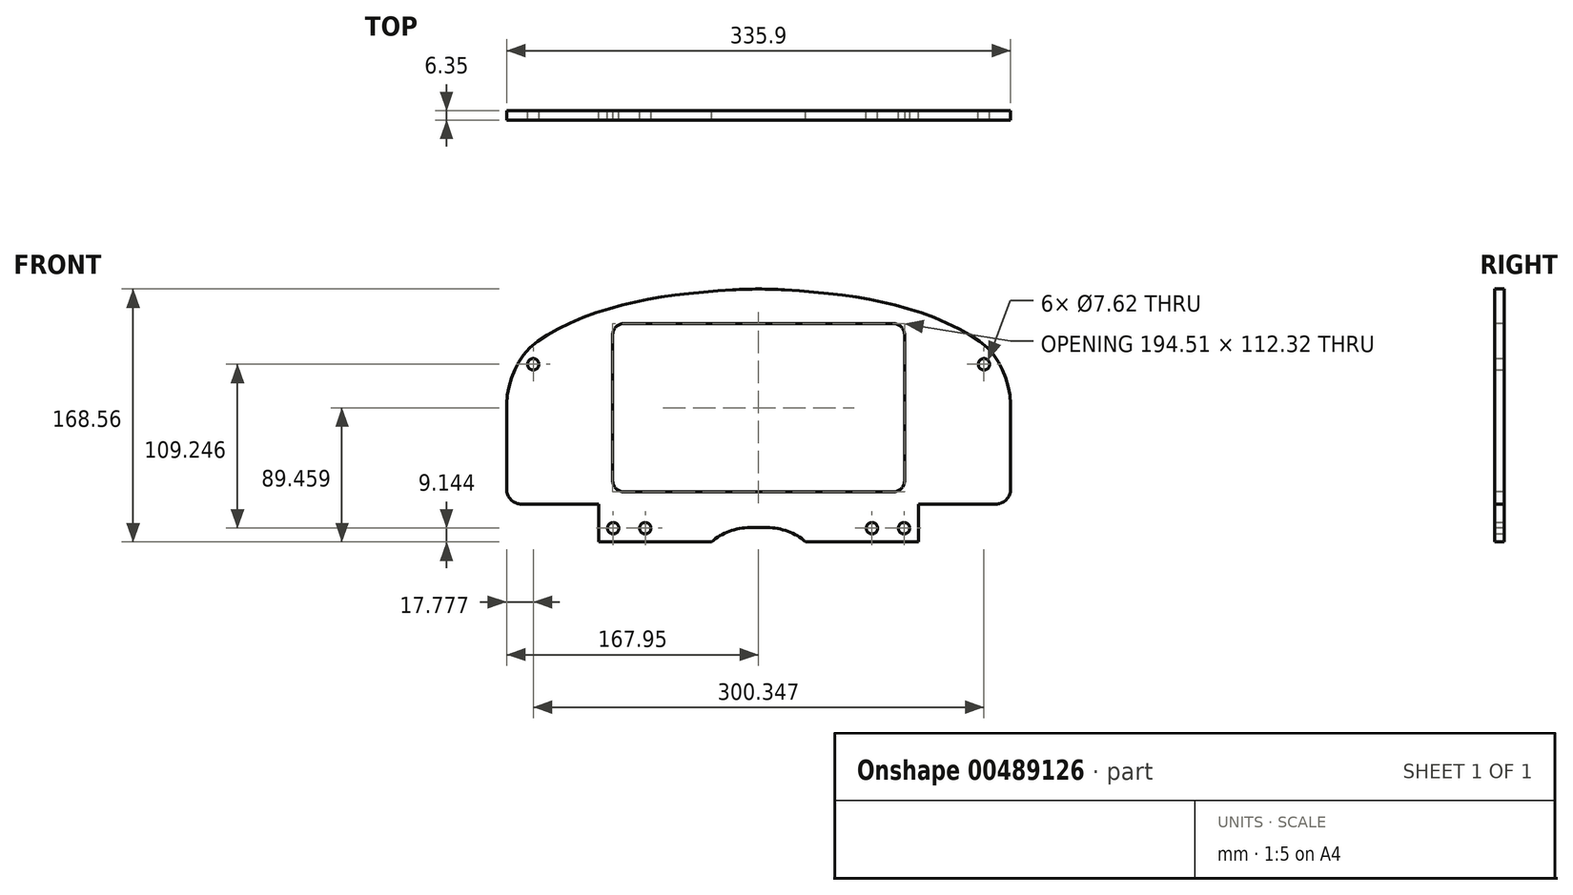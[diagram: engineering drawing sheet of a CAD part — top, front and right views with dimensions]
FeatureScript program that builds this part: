
annotation { "Feature Type Name" : "Feature", "Feature Type Description" : "" }
export const myFeature = defineFeature(function(context is Context, id is Id, definition is map)
    precondition{}
    {
        {
            var Q0;
            Q0=qCreatedBy(makeId("Front.planeOp"),FACE);
            var sketch = newSketch(context, id + "F0", { "sketchPlane" : qUnion([Q0])});
            skLineSegment(sketch, "E0", {"start": v(-160.02, 0) * mm, "end": v(160.02, 0) * mm});
            skLineSegment(sketch, "E1", {"start": v(-31.43, -64.77) * mm, "end": v(-106.52, -64.77) * mm});
            skLineSegment(sketch, "E2", {"start": v(-106.52, -64.77) * mm, "end": v(-106.52, -39.6) * mm});
            skLineSegment(sketch, "E3", {"start": v(-106.52, -39.6) * mm, "end": v(-167.95, -39.6) * mm});
            skLineSegment(sketch, "E4", {"start": v(-167.95, -39.6) * mm, "end": v(-167.95, 26.96) * mm});
            skLineSegment(sketch, "E5", {"start": v(0, 0) * mm, "end": v(0, 118.4) * mm, "construction": true});
            skLineSegment(sketch, "E6", {"start": v(0, 118.4) * mm, "end": v(0, -81.7) * mm, "construction": true});
            skLineSegment(sketch, "E7", {"start": v(0, -55.25) * mm, "end": v(-5.83, -55.25) * mm});
            skArc(sketch, "E8", {"start": v(-5.83, -55.25) * mm, "mid": v(-19.49, -57.7) * mm, "end": v(-31.43, -64.77) * mm});
            skFitSpline(sketch, "E9", {"points": [v(0, 104.31) * mm, v(-59.59, 99.2) * mm, v(-109.08, 87.67) * mm, v(-150.03, 66.77) * mm, v(-162.83, 48.85) * mm, v(-167.95, 26.96) * mm], "startDerivative": vector(-246.06, -15.43) * mm, "endDerivative": vector(0, -151.52) * mm});
            skFitSpline(sketch, "E10.MirrorCS", {"points": [v(0, 104.31) * mm, v(59.59, 99.2) * mm, v(109.08, 87.67) * mm, v(150.03, 66.77) * mm, v(162.83, 48.85) * mm, v(167.95, 26.96) * mm], "startDerivative": vector(246.06, -15.43) * mm, "endDerivative": vector(0, -151.52) * mm});
            skLineSegment(sketch, "E11.MirrorCS", {"start": v(167.95, -39.6) * mm, "end": v(167.95, 26.96) * mm});
            skLineSegment(sketch, "E12.MirrorCS", {"start": v(106.52, -39.6) * mm, "end": v(167.95, -39.6) * mm});
            skLineSegment(sketch, "E13.MirrorCS", {"start": v(106.52, -64.77) * mm, "end": v(106.52, -39.6) * mm});
            skLineSegment(sketch, "E14.MirrorCS", {"start": v(31.43, -64.77) * mm, "end": v(106.52, -64.77) * mm});
            skArc(sketch, "E15.MirrorCS", {"start": v(5.83, -55.25) * mm, "mid": v(19.49, -57.7) * mm, "end": v(31.43, -64.77) * mm});
            skLineSegment(sketch, "E16.MirrorCS", {"start": v(0, -55.25) * mm, "end": v(5.83, -55.25) * mm});
            skCircle(sketch, "E17", {"center": v(-96.87, -55.63) * mm, "radius": 3.81 * mm});
            skCircle(sketch, "E18", {"center": v(-75.53, -55.63) * mm, "radius": 3.81 * mm});
            skCircle(sketch, "E19", {"center": v(75.53, -55.63) * mm, "radius": 3.81 * mm});
            skCircle(sketch, "E20", {"center": v(96.87, -55.63) * mm, "radius": 3.81 * mm});
            skCircle(sketch, "E21", {"center": v(150.17, 53.62) * mm, "radius": 3.81 * mm});
            skCircle(sketch, "E22", {"center": v(-150.17, 53.62) * mm, "radius": 3.81 * mm});
            skSolve(sketch);
        }
        {
            var Q0;
            Q0=makeQuery(id+"F0.imprint","IMPRINT",FACE,{"disambiguationData":[TD([[makeQuery(id+"F0.imprint","IMPRINT",EDGE,{"derivedFrom":sQuery(id+"F0.wireOp",EDGE,"E1")}),-1.0]])]});
            extrude(context, id + "F1", {"entities" : qUnion([Q0]), "depth" : 6.35 * mm});
        }
        {
            var Q0;
            Q0=makeQuery(id+"F1.opExtrude","SWEPT_EDGE",EDGE,{"disambiguationData":[OSD([sQuery(id+"F0.wireOp",EDGE,"E11.MirrorCS"),sQuery(id+"F0.wireOp",EDGE,"E12.MirrorCS")])]});
            var Q1;
            Q1=makeQuery(id+"F1.opExtrude","SWEPT_EDGE",EDGE,{"disambiguationData":[OSD([sQuery(id+"F0.wireOp",EDGE,"E3"),sQuery(id+"F0.wireOp",EDGE,"E4")])]});
            fillet(context, id + "F2", {"entities" : qUnion([Q0, Q1]), "radius" : 10.16 * mm, "tangentPropagation" : true, "allowEdgeOverflow" : false});
        }
        {
            var Q0;
            Q0=makeQuery(id+"F1.opExtrude","CAP_FACE",FACE,{"disambiguationData":[OSD([sQuery(id+"F0.wireOp",EDGE,"E1"),sQuery(id+"F0.wireOp",EDGE,"E2"),sQuery(id+"F0.wireOp",EDGE,"E3"),sQuery(id+"F0.wireOp",EDGE,"E4"),sQuery(id+"F0.wireOp",EDGE,"E7"),sQuery(id+"F0.wireOp",EDGE,"E8"),sQuery(id+"F0.wireOp",EDGE,"E9"),sQuery(id+"F0.wireOp",EDGE,"E10.MirrorCS"),sQuery(id+"F0.wireOp",EDGE,"E11.MirrorCS"),sQuery(id+"F0.wireOp",EDGE,"E12.MirrorCS"),sQuery(id+"F0.wireOp",EDGE,"E13.MirrorCS"),sQuery(id+"F0.wireOp",EDGE,"E14.MirrorCS"),sQuery(id+"F0.wireOp",EDGE,"E15.MirrorCS"),sQuery(id+"F0.wireOp",EDGE,"E16.MirrorCS"),sQuery(id+"F0.wireOp",EDGE,"E17"),sQuery(id+"F0.wireOp",EDGE,"E18"),sQuery(id+"F0.wireOp",EDGE,"E19"),sQuery(id+"F0.wireOp",EDGE,"E20"),sQuery(id+"F0.wireOp",EDGE,"E21"),sQuery(id+"F0.wireOp",EDGE,"E22")])],"isStart":false});
            var sketch = newSketch(context, id + "F3", { "sketchPlane" : qUnion([Q0])});
            skLineSegment(sketch, "E23.bottom", {"start": v(-89.48, 80.09) * mm, "end": v(89.48, 80.09) * mm, "construction": true});
            skLineSegment(sketch, "E23.top", {"start": v(-89.48, -30.7) * mm, "end": v(89.48, -30.7) * mm, "construction": true});
            skLineSegment(sketch, "E23.left", {"start": v(-96.5, 73.08) * mm, "end": v(-96.5, -23.7) * mm, "construction": true});
            skLineSegment(sketch, "E23.right", {"start": v(96.5, 73.08) * mm, "end": v(96.5, -23.7) * mm, "construction": true});
            skPoint(sketch, "E24.visualSharp", {"position": v(-96.5, 80.09) * mm});
            skArc(sketch, "E24.filletArc", {"start": v(-89.48, 80.09) * mm, "mid": v(-94.44, 78.03) * mm, "end": v(-96.5, 73.08) * mm, "construction": true});
            skPoint(sketch, "E25.visualSharp", {"position": v(-96.5, -30.7) * mm});
            skArc(sketch, "E25.filletArc", {"start": v(-96.5, -23.7) * mm, "mid": v(-94.44, -28.66) * mm, "end": v(-89.48, -30.7) * mm, "construction": true});
            skPoint(sketch, "E26.visualSharp", {"position": v(96.5, -30.7) * mm});
            skArc(sketch, "E26.filletArc", {"start": v(89.48, -30.7) * mm, "mid": v(94.44, -28.66) * mm, "end": v(96.5, -23.7) * mm, "construction": true});
            skPoint(sketch, "E27.visualSharp", {"position": v(96.5, 80.09) * mm});
            skArc(sketch, "E27.filletArc", {"start": v(96.5, 73.08) * mm, "mid": v(94.44, 78.03) * mm, "end": v(89.48, 80.09) * mm, "construction": true});
            skLineSegment(sketch, "E28.0", {"start": v(-89.48, -31.47) * mm, "end": v(89.48, -31.47) * mm});
            skLineSegment(sketch, "E28.1", {"start": v(-89.48, 80.85) * mm, "end": v(89.48, 80.85) * mm});
            skArc(sketch, "E28.2", {"start": v(97.26, 73.08) * mm, "mid": v(94.98, 78.57) * mm, "end": v(89.48, 80.85) * mm});
            skLineSegment(sketch, "E28.3", {"start": v(97.26, 73.08) * mm, "end": v(97.26, -23.7) * mm});
            skArc(sketch, "E28.4", {"start": v(89.48, -31.47) * mm, "mid": v(94.98, -29.2) * mm, "end": v(97.26, -23.7) * mm});
            skArc(sketch, "E29.0", {"start": v(-97.26, -23.7) * mm, "mid": v(-94.98, -29.2) * mm, "end": v(-89.48, -31.47) * mm});
            skLineSegment(sketch, "E29.1", {"start": v(-97.26, 73.08) * mm, "end": v(-97.26, -23.7) * mm});
            skArc(sketch, "E29.2", {"start": v(-89.48, 80.85) * mm, "mid": v(-94.98, 78.57) * mm, "end": v(-97.26, 73.08) * mm});
            skSolve(sketch);
        }
        {
            var Q0;
            Q0=makeQuery(id+"F3.imprint","IMPRINT",FACE,{"disambiguationData":[TD([[makeQuery(id+"F3.imprint","IMPRINT",EDGE,{"derivedFrom":sQuery(id+"F3.wireOp",EDGE,"E28.0")}),1.0]])]});
            extrude(context, id + "F4", {"entities" : qUnion([Q0]), "operationType" : NewBodyOperationType.REMOVE, "oppositeDirection" : true, "depth" : 25.4 * mm});
        }
        {
            var Q0;
            Q0=makeQuery(id+"F1.opExtrude","SWEPT_EDGE",EDGE,{"disambiguationData":[OSD([sQuery(id+"F0.wireOp",EDGE,"E9"),sQuery(id+"F0.wireOp",EDGE,"E10.MirrorCS")])]});
            fillet(context, id + "F5", {"entities" : qUnion([Q0]), "radius" : 254 * mm, "tangentPropagation" : true, "allowEdgeOverflow" : false});
        }
    });
